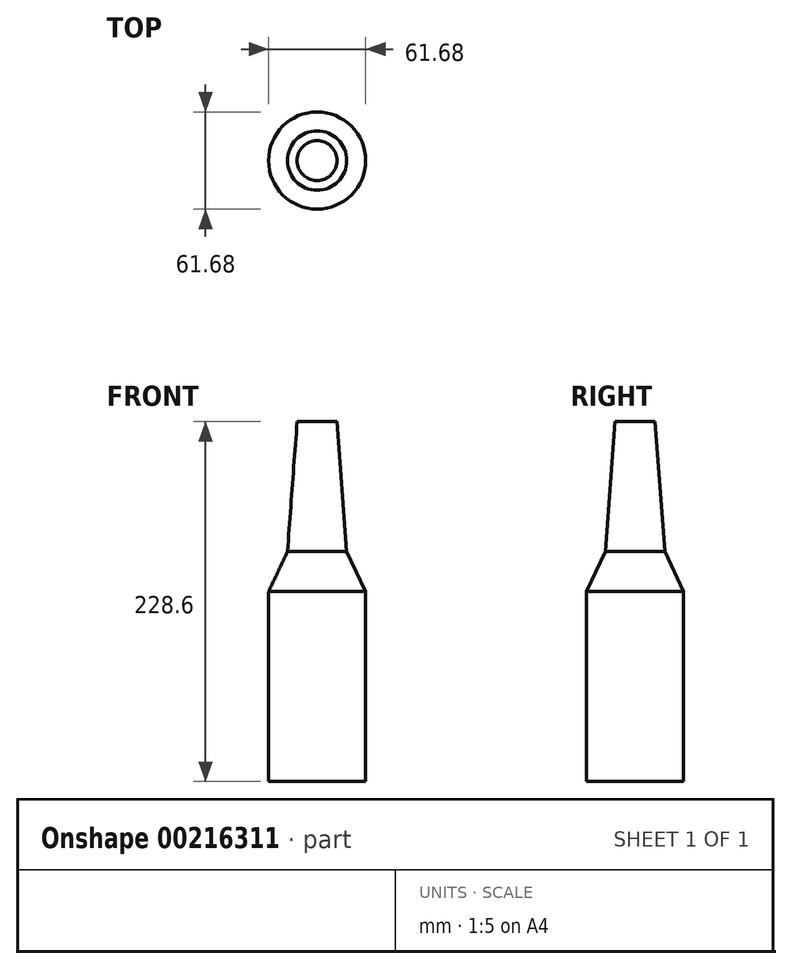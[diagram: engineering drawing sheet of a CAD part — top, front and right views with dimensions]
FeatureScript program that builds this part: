
annotation { "Feature Type Name" : "Feature", "Feature Type Description" : "" }
export const myFeature = defineFeature(function(context is Context, id is Id, definition is map)
    precondition{}
    {
        {
            var Q0;
            Q0=qCreatedBy(makeId("Front.planeOp"),FACE);
            var sketch = newSketch(context, id + "F0", { "sketchPlane" : qUnion([Q0])});
            skLineSegment(sketch, "E0", {"start": v(0, 133.6) * mm, "end": v(0, -170.6) * mm, "construction": true});
            skLineSegment(sketch, "E1", {"start": v(0, 107.95) * mm, "end": v(99.57, 107.95) * mm, "construction": true});
            skLineSegment(sketch, "E2", {"start": v(0, 107.95) * mm, "end": v(-128.57, 107.95) * mm, "construction": true});
            skLineSegment(sketch, "E3", {"start": v(-128.57, -120.65) * mm, "end": v(99.57, -120.65) * mm, "construction": true});
            skLineSegment(sketch, "E4", {"start": v(-128.57, 25.4) * mm, "end": v(99.57, 25.4) * mm, "construction": true});
            skLineSegment(sketch, "E5", {"start": v(-128.57, 0) * mm, "end": v(99.57, 0) * mm, "construction": true});
            skLineSegment(sketch, "E6", {"start": v(0, 107.95) * mm, "end": v(12.7, 107.95) * mm});
            skLineSegment(sketch, "E7", {"start": v(12.7, 107.95) * mm, "end": v(18.8, 25.4) * mm});
            skLineSegment(sketch, "E8", {"start": v(18.8, 25.4) * mm, "end": v(30.84, 0) * mm});
            skLineSegment(sketch, "E9", {"start": v(30.84, 0) * mm, "end": v(30.84, -120.65) * mm});
            skLineSegment(sketch, "E10", {"start": v(30.84, -120.65) * mm, "end": v(0, -120.65) * mm});
            skLineSegment(sketch, "E11", {"start": v(0, -120.65) * mm, "end": v(0, 107.95) * mm});
            skSolve(sketch);
        }
        {
            var Q0;
            Q0=makeQuery(id+"F0.imprint","IMPRINT",FACE,{"disambiguationData":[TD([[makeQuery(id+"F0.imprint","IMPRINT",EDGE,{"derivedFrom":sQuery(id+"F0.wireOp",EDGE,"E6")}),-1.0]])]});
            var Q1;
            Q1=sQuery(id+"F0.wireOp",EDGE,"E11");
            revolve(context, id + "F1", {"entities" : qUnion([Q0]), "axis" : qUnion([Q1]), "revolveType" : RevolveType.FULL});
        }
    });
